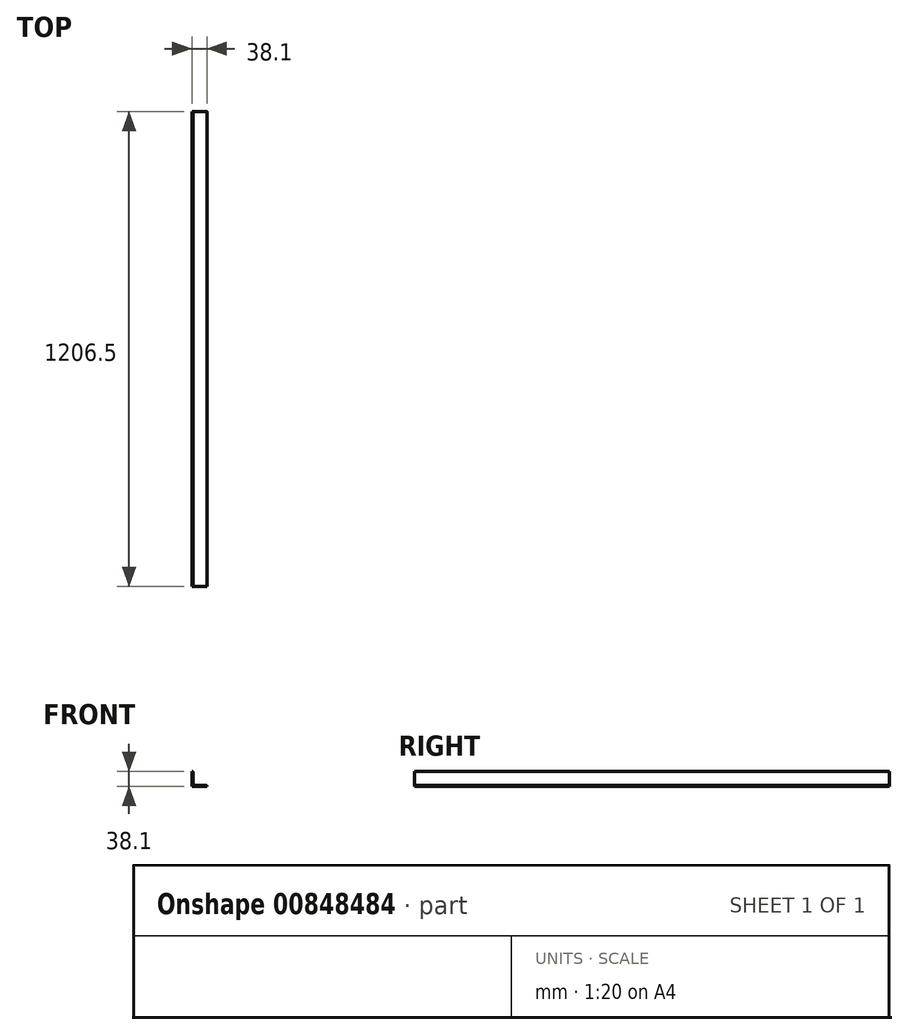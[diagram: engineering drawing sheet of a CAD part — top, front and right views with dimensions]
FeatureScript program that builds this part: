
annotation { "Feature Type Name" : "Feature", "Feature Type Description" : "" }
export const myFeature = defineFeature(function(context is Context, id is Id, definition is map)
    precondition{}
    {
        {
            var Q0;
            Q0=qCreatedBy(makeId("Front.planeOp"),FACE);
            var sketch = newSketch(context, id + "F0", { "sketchPlane" : qUnion([Q0])});
            skLineSegment(sketch, "E0", {"start": v(0, 0) * mm, "end": v(38.1, 0) * mm});
            skLineSegment(sketch, "E1", {"start": v(0, 0) * mm, "end": v(0, 38.1) * mm});
            skLineSegment(sketch, "E2", {"start": v(0, 38.1) * mm, "end": v(0, 38.1) * mm});
            skLineSegment(sketch, "E3", {"start": v(3.18, 34.93) * mm, "end": v(3.18, 3.18) * mm});
            skLineSegment(sketch, "E4", {"start": v(38.1, 0) * mm, "end": v(38.1, 0) * mm});
            skLineSegment(sketch, "E5", {"start": v(34.93, 3.18) * mm, "end": v(3.18, 3.18) * mm});
            skPoint(sketch, "E6.orphan", {"position": v(3.18, 0) * mm});
            skPoint(sketch, "E7.visualSharp", {"position": v(3.18, 38.1) * mm});
            skArc(sketch, "E7.filletArc", {"start": v(3.18, 34.93) * mm, "mid": v(2.25, 37.17) * mm, "end": v(0, 38.1) * mm});
            skPoint(sketch, "E8.visualSharp", {"position": v(38.1, 3.18) * mm});
            skArc(sketch, "E8.filletArc", {"start": v(38.1, 0) * mm, "mid": v(37.17, 2.25) * mm, "end": v(34.93, 3.17) * mm});
            skSolve(sketch);
        }
        {
            var Q0;
            Q0=makeQuery(id+"F0.imprint","IMPRINT",FACE,{"disambiguationData":[TD([[makeQuery(id+"F0.imprint","IMPRINT",EDGE,{"derivedFrom":sQuery(id+"F0.wireOp",EDGE,"E0")}),1.0]])]});
            extrude(context, id + "F1", {"entities" : qUnion([Q0]), "oppositeDirection" : true, "depth" : 1206.5 * mm, "offsetDistance" : 25.4 * mm});
        }
    });
